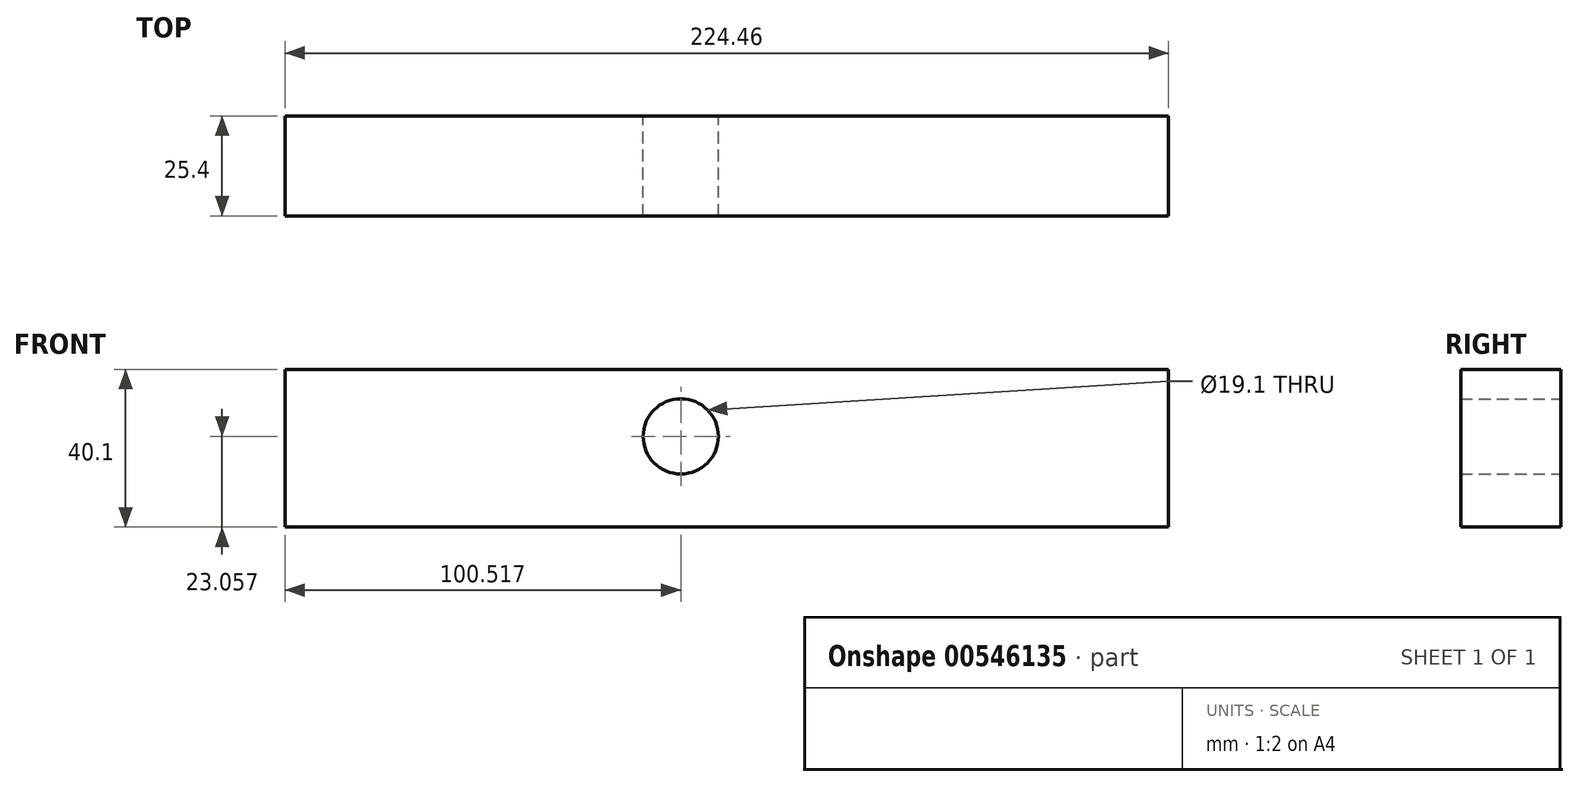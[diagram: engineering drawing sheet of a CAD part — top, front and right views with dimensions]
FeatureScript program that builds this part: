
annotation { "Feature Type Name" : "Feature", "Feature Type Description" : "" }
export const myFeature = defineFeature(function(context is Context, id is Id, definition is map)
    precondition{}
    {
        {
            var Q0;
            Q0=qCreatedBy(makeId("Front.planeOp"),FACE);
            var sketch = newSketch(context, id + "F0", { "sketchPlane" : qUnion([Q0])});
            skLineSegment(sketch, "E0.bottom", {"start": v(-97.11, -4.6) * mm, "end": v(127.35, -4.6) * mm});
            skLineSegment(sketch, "E0.top", {"start": v(-97.11, 35.49) * mm, "end": v(127.35, 35.49) * mm});
            skLineSegment(sketch, "E0.left", {"start": v(-97.11, -4.6) * mm, "end": v(-97.11, 35.49) * mm});
            skLineSegment(sketch, "E0.right", {"start": v(127.35, -4.6) * mm, "end": v(127.35, 35.49) * mm});
            skCircle(sketch, "E1", {"center": v(3.4, 18.45) * mm, "radius": 9.55 * mm});
            skSolve(sketch);
        }
        {
            var Q0;
            Q0=makeQuery(id+"F0.imprint","IMPRINT",FACE,{"disambiguationData":[TD([[makeQuery(id+"F0.imprint","IMPRINT",EDGE,{"derivedFrom":sQuery(id+"F0.wireOp",EDGE,"E0.bottom")}),1.0]])]});
            extrude(context, id + "F1", {"entities" : qUnion([Q0]), "depth" : 25.4 * mm, "offsetDistance" : 25.4 * mm});
        }
    });
